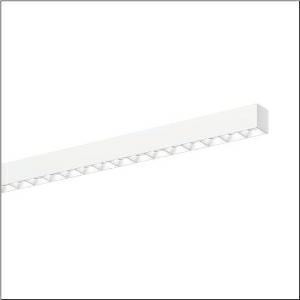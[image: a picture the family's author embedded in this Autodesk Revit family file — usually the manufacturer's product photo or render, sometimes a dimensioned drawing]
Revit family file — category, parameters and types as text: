
# Revit family: silica_21_51mx26dc3awb
name_source: partatom
category: Lighting Fixtures
units: mm (PartAtom-declared; Revit-internal decimal feet)

## family parameters
Cut with Voids When Loaded = No
Host = Face
Light Source = No
Part Type = Normal
Room Calculation Point = No
Round Connector Dimension = Use Diameter
Shared = No

## types (1)
- --- (1 x LED, 10800 lm, 63.6 W, 3000K)
    Apparent Load = 64 VA
    CIE Flux Codes = 83 98 100 100 100
    Color Rendering = 80
    Color Temperature = 3000K
    Default Elevation = 1800 mm
    Description = Silica 21, office luminaire, primary light control with darklight reflector, of PMMA, white, CAT 2 (L<= 3000cd/m²), light emission: direct distribution, primary light characteristic: symmetric, installation type: surface-mounted, LED, rated luminous flux: 10.800lm, luminous efficacy: 170lm/W, light colour: 830, colour temperature: 3000K, control gear: DALI 2, with terminal, 3+2-pole, max. 2.5mm², mains connection: 220..240V, AC, 50/60Hz, rated input power: 63.6W, luminaire housing, of aluminium, traffic white (RAL 9016), length: 3.004mm, width: 53mm, height: 53mm, protection rating (complete): IP20, insulation class (complete): insulation class I (protective earthing), certification: CE, permissible operating ambient temperature: 0..+35°C, standard: EN 50419, packaging unit: 1 piece
    Height = 53 mm
    Lamp = 1 x LED
    Lamp Light Flux = 10800 lm
    Lamp Power = 63.6 W
    Lamp count = 1
    Length = 3004 mm
    Luminous efficacy = 170 lm/W
    Manufacturer = Siteco
    ModVariant = No
    Model = 51MX26DC3AWB
    Mounting Place = Ceiling
    Mounting Type = Surface mounted
    Number of Poles = 1
    OnlyDefault = Yes
    Power Factor = 1
    Product Name = Silica 21
    Product group = office luminaire | ceiling mounted
    ProductGroupID = 301
    Protection Class = Protection class I
    Protection Degree = IP 20
    RLX_Detail_Level = 1
    RLX_Emergency_Light_Flux = 0 lm
    RLX_Emergency_Type = 0
    RLX_Emergency_Type_DB = No
    RlxData = <blob elided: 58917 chars, md5=54219476>
    Socket = socket
    Standby Power = 0 W
    System Light Flux = 10800 lm
    System Power = 64 W
    Type Comments = factory setting: luminous flux: 100 % | dim-lin: 254 | 360 mA
    Type Image = l_1335934.jpg
    URL = http://relux.com
    VarID = @adj_124335
    Voltage = 0 V
    Weight = 0.00 kg
    Width = 53 mm

## geometry (parser evidence)
native form markers: Blend x4, Sweep x11
no freeform markers — native parametric forms only
